# Revit family: Doors_Security_Troax_Fence-Door_UR-350
name_source: partatom
category: Specialty Equipment
revit_build: Autodesk Revit 2017 (Build: 20190508_0315(x64)
units: mm (PartAtom-declared; Revit-internal decimal feet)

## family parameters
Always vertical = Yes
Cut with Voids When Loaded = No
OmniClass Number = 23.25.40.21.21.11
OmniClass Title = Swinging Gates
Part Type = Normal
Room Calculation Point = No
Round Connector Dimension = Use Diameter
Shared = No
Work Plane-Based = No

## types (2) — shared parameters
AssetType = Fixed
BIMObjectName = Doors_Security_Troax_Fence-Door_UR-350
Brand = Troax
Category = Doors
Color = Grey
Constituents = Cut profile: various length to use after cut height on site; End profile UR/UX L=2200 to use after cut panel length on site; U-profile UR 19x19x2200 various length to use after cut on site
Description = The UR 350 Padlock door is primarily designed to be used together with Troax UR 350 mesh panel. UR 350 doors and panels are ideal for secure environments where the risk of break-ins is low. The door leaf has a 30x20 mm steel tube frame and two horizontal tubes to create strength and stability. The 50x50 mesh aperture also makes it virtually impossible for a hand to reach through the mesh. Doors are supplied preassembled and are ready for installation.
DurationUnit = Year
Features = The door leaf has a 30x20 mm steel tube frame and two horizontal tubes to create strength and stability. The 50x50 mesh aperture also makes it virtually impossible for a hand to reach through the mesh. Doors are supplied preassembled and are ready for installation.
Finish = Powder coated as standard with a grey RAL 7037 finish. However other RAL colors are available upon request.
FurniturePanelType = Other
HasOpening = Yes
IfcExportAs = IfcSystemFurnitureElementTypePanel
IfcExportType = DOOR
MainColor = Grey
Manufacturer = Troax
ManufacturerName = Troax
ManufacturerURL = https://www.troax.com
Material = Carbon steel
NBSDescription = Metal doorsets
NBSReference = 45-25-28/344
NominalDepth = 76 mm  [stored 0.249344 ft]
NominalHeight = 2200 mm
ProductDatasheet = https://www.troax.com
ProductInformation = Troax Classic is an excellent choice of mesh partition for storage spaces in apartment buildings, cellars and attics that already have exterior protection or where there is a low risk of tampering.
Revision = 2
Shape = Sculptured
URL = https://www.troax.com
Uniclass2 = Pr_30_59_23_11
Uniclass2015Description = Carbon steel door frames
Uniclass2015Reference = Pr_30_59_23_11
Version = 1
VersionDate = 01/07/2020
WallPanelMainMaterial = Steel, Carbon
WarrantyDurationUnit = Year
zero-valued in all types: Cost, NominalThickness

## per-type parameters (varying)
| type | ConvergoRefNr | DoorType | Name | NominalWidth | Size |
| Troax classic UR 350 900mm | 0054-1811-0033-SE | Door ur350 900 | Troax_Fence-Door_UR-350_900 | 918 mm  [stored 3.01181 ft] | 76x2200x918 mm |
| Troax classic UR 350 750mm | 0054-1811-0032-SE | Door ur350 750 | Troax_Fence-Door_UR-350_750 | 768 mm  [stored 2.51969 ft] | 76x2200x768 mm |

note: column(s) folded — value = type name in every type: Model

note: [stored X ft] marks values corroborated as IEEE doubles in the binary element streams (Revit-internal decimal feet)

## geometry (parser evidence)
native form markers: Blend x4, Sweep x6
no freeform markers — native parametric forms only
